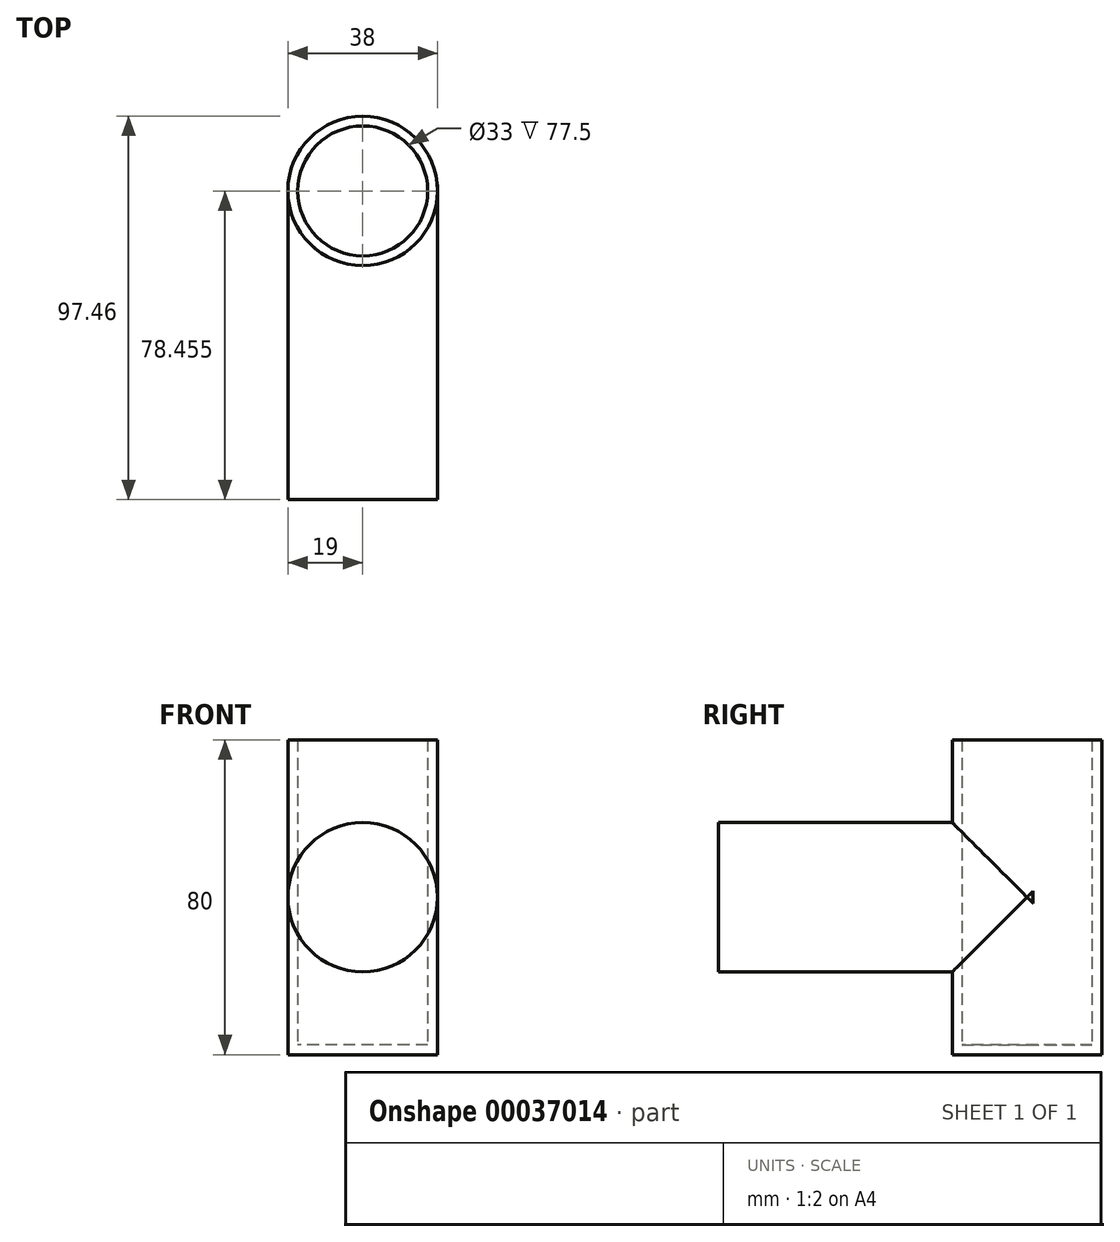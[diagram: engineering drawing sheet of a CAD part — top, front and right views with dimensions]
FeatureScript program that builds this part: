
annotation { "Feature Type Name" : "Feature", "Feature Type Description" : "" }
export const myFeature = defineFeature(function(context is Context, id is Id, definition is map)
    precondition{}
    {
        {
            var Q0;
            Q0=qCreatedBy(makeId("Front.planeOp"),FACE);
            var sketch = newSketch(context, id + "F0", { "sketchPlane" : qUnion([Q0])});
            skCircle(sketch, "E0", {"center": v(0, 0) * mm, "radius": 19 * mm});
            skSolve(sketch);
        }
        {
            var Q0;
            Q0 = qSketchRegion(id + "F0", true);
            extrude(context, id + "F1", {"entities" : qUnion([Q0]), "oppositeDirection" : true, "depth" : 80 * mm});
        }
        {
            var Q0;
            Q0=qCreatedBy(makeId("Top.planeOp"),FACE);
            var sketch = newSketch(context, id + "F2", { "sketchPlane" : qUnion([Q0])});
            skCircle(sketch, "E1", {"center": v(0, 78.46) * mm, "radius": 19 * mm});
            skSolve(sketch);
        }
        {
            var Q0;
            Q0 = qSketchRegion(id + "F2", true);
            extrude(context, id + "F3", {"entities" : qUnion([Q0]), "operationType" : NewBodyOperationType.ADD, "endBound" : BoundingType.SYMMETRIC, "depth" : 80 * mm});
        }
        {
            var Q0;
            Q0=makeQuery(id+"F3.opExtrude","CAP_FACE",FACE,{"disambiguationData":[OSD([sQuery(id+"F2.wireOp",EDGE,"E1")])],"isStart":false});
            shell(context, id + "F4", {"entities" : qUnion([Q0]), "thickness" : 2.5 * mm});
        }
    });
